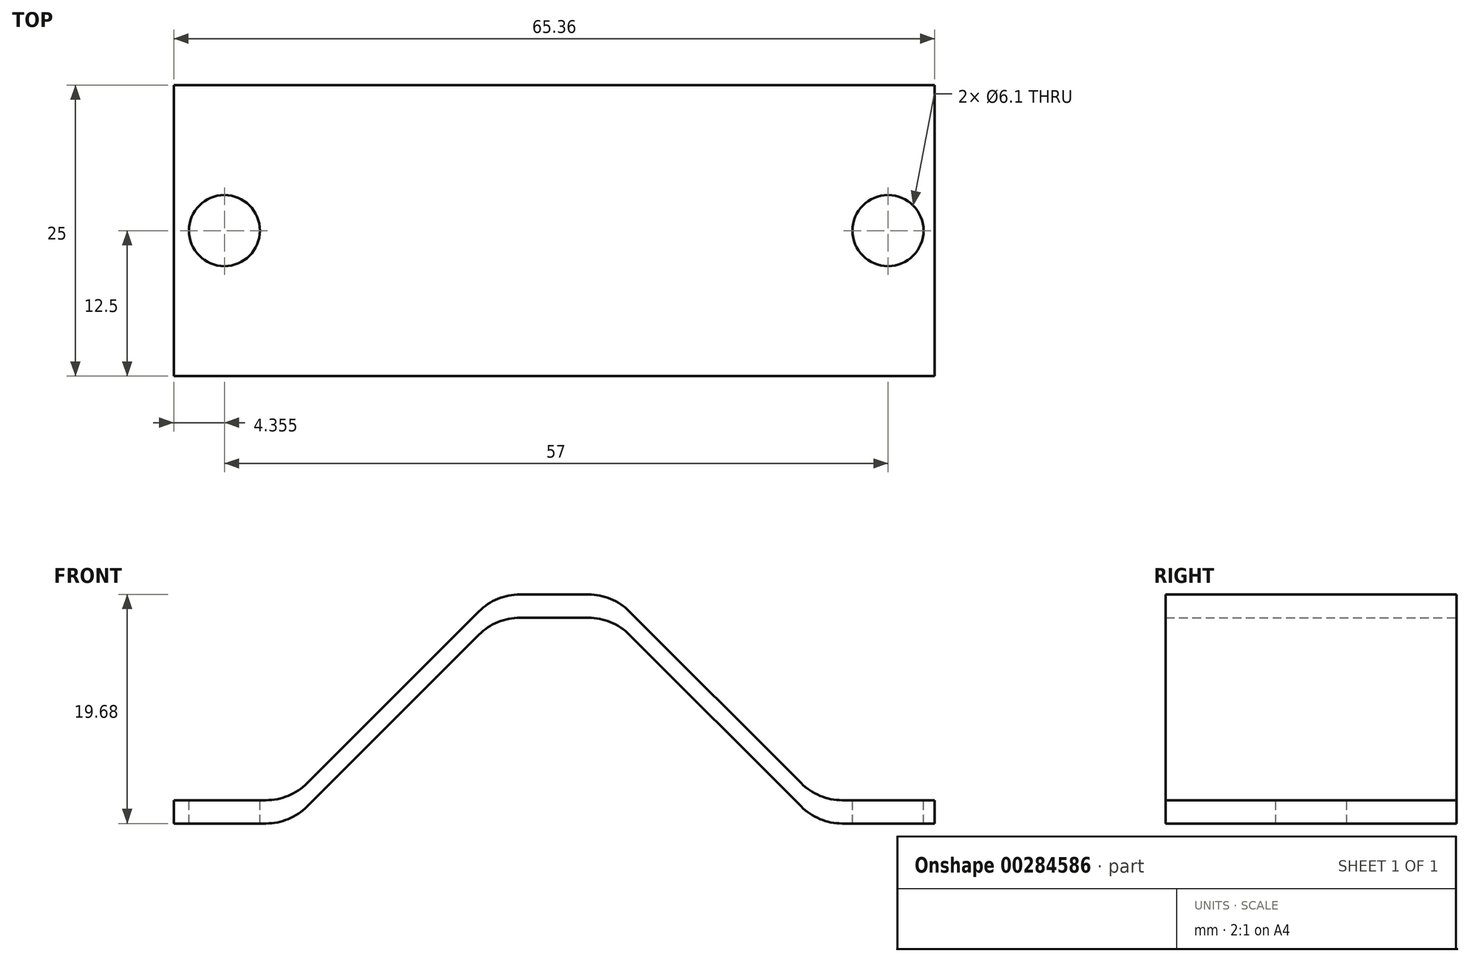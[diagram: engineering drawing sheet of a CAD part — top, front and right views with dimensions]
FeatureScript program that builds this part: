
annotation { "Feature Type Name" : "Feature", "Feature Type Description" : "" }
export const myFeature = defineFeature(function(context is Context, id is Id, definition is map)
    precondition{}
    {
        {
            var Q0;
            Q0=qCreatedBy(makeId("Front.planeOp"),FACE);
            var sketch = newSketch(context, id + "F0", { "sketchPlane" : qUnion([Q0])});
            skLineSegment(sketch, "E0", {"start": v(0, 0) * mm, "end": v(7.93, 0) * mm});
            skLineSegment(sketch, "E1", {"start": v(11.46, 1.46) * mm, "end": v(26.21, 16.21) * mm});
            skLineSegment(sketch, "E2", {"start": v(29.75, 17.68) * mm, "end": v(35.6, 17.68) * mm});
            skLineSegment(sketch, "E3", {"start": v(39.14, 16.21) * mm, "end": v(53.9, 1.46) * mm});
            skLineSegment(sketch, "E4", {"start": v(57.43, 0) * mm, "end": v(65.36, 0) * mm});
            skLineSegment(sketch, "E5", {"start": v(65.36, 0) * mm, "end": v(65.36, -2) * mm});
            skLineSegment(sketch, "E6", {"start": v(65.36, -2) * mm, "end": v(57.43, -2) * mm});
            skLineSegment(sketch, "E7", {"start": v(53.9, -0.54) * mm, "end": v(39.14, 14.21) * mm});
            skLineSegment(sketch, "E8", {"start": v(35.6, 15.68) * mm, "end": v(29.75, 15.68) * mm});
            skLineSegment(sketch, "E9", {"start": v(26.21, 14.21) * mm, "end": v(11.46, -0.54) * mm});
            skLineSegment(sketch, "E10", {"start": v(7.93, -2) * mm, "end": v(0, -2) * mm});
            skLineSegment(sketch, "E11", {"start": v(0, -2) * mm, "end": v(0, 0) * mm});
            skPoint(sketch, "E12.visualSharp", {"position": v(27.68, 15.68) * mm});
            skArc(sketch, "E12.filletArc", {"start": v(29.75, 15.68) * mm, "mid": v(27.84, 15.3) * mm, "end": v(26.21, 14.21) * mm});
            skPoint(sketch, "E13.visualSharp", {"position": v(27.68, 17.68) * mm});
            skArc(sketch, "E13.filletArc", {"start": v(29.75, 17.68) * mm, "mid": v(27.84, 17.3) * mm, "end": v(26.21, 16.21) * mm});
            skPoint(sketch, "E14.visualSharp", {"position": v(37.68, 15.68) * mm});
            skArc(sketch, "E14.filletArc", {"start": v(39.14, 14.21) * mm, "mid": v(37.52, 15.3) * mm, "end": v(35.6, 15.68) * mm});
            skPoint(sketch, "E15.visualSharp", {"position": v(37.68, 17.68) * mm});
            skArc(sketch, "E15.filletArc", {"start": v(39.14, 16.21) * mm, "mid": v(37.52, 17.3) * mm, "end": v(35.6, 17.68) * mm});
            skPoint(sketch, "E16.visualSharp", {"position": v(10, 0) * mm});
            skArc(sketch, "E16.filletArc", {"start": v(7.93, 0) * mm, "mid": v(9.84, 0.38) * mm, "end": v(11.46, 1.46) * mm});
            skPoint(sketch, "E17.visualSharp", {"position": v(10, -2) * mm});
            skArc(sketch, "E17.filletArc", {"start": v(7.93, -2) * mm, "mid": v(9.84, -1.62) * mm, "end": v(11.46, -0.54) * mm});
            skPoint(sketch, "E18.visualSharp", {"position": v(55.36, -2) * mm});
            skArc(sketch, "E18.filletArc", {"start": v(53.9, -0.54) * mm, "mid": v(55.51, -1.62) * mm, "end": v(57.43, -2) * mm});
            skPoint(sketch, "E19.visualSharp", {"position": v(55.36, 0) * mm});
            skArc(sketch, "E19.filletArc", {"start": v(53.9, 1.46) * mm, "mid": v(55.51, 0.38) * mm, "end": v(57.43, 0) * mm});
            skSolve(sketch);
        }
        {
            var Q0;
            Q0=makeQuery(id+"F0.imprint","IMPRINT",FACE,{"disambiguationData":[TD([[makeQuery(id+"F0.imprint","IMPRINT",EDGE,{"derivedFrom":sQuery(id+"F0.wireOp",EDGE,"E0")}),-1.0]])]});
            extrude(context, id + "F1", {"entities" : qUnion([Q0]), "depth" : 25 * mm});
        }
        {
            var Q0;
            Q0=makeQuery(id+"F1.opExtrude","SWEPT_FACE",FACE,{"disambiguationData":[OSD([sQuery(id+"F0.wireOp",EDGE,"E4")])]});
            var sketch = newSketch(context, id + "F2", { "sketchPlane" : qUnion([Q0])});
            skLineSegment(sketch, "E20", {"start": v(65.36, -12.5) * mm, "end": v(61.36, -12.5) * mm, "construction": true});
            skLineSegment(sketch, "E21", {"start": v(0, 0) * mm, "end": v(0, -12.5) * mm, "construction": true});
            skLineSegment(sketch, "E22", {"start": v(0, -12.5) * mm, "end": v(4.36, -12.5) * mm, "construction": true});
            skPoint(sketch, "E23", {"position": v(4.36, -12.5) * mm});
            skPoint(sketch, "E24", {"position": v(61.36, -12.5) * mm});
            skSolve(sketch);
        }
        {
            var Q0;
            Q0=sQuery(id+"F2.wireOp",VERTEX,"E23");
            var Q1;
            Q1=sQuery(id+"F2.wireOp",VERTEX,"E24");
            var Q2;
            Q2=makeQuery(id+"F1.opExtrude","SWEPT_BODY",BODY,{"disambiguationData":[OSD([sQuery(id+"F0.wireOp",EDGE,"E0"),sQuery(id+"F0.wireOp",EDGE,"E1"),sQuery(id+"F0.wireOp",EDGE,"E2"),sQuery(id+"F0.wireOp",EDGE,"E3"),sQuery(id+"F0.wireOp",EDGE,"E4"),sQuery(id+"F0.wireOp",EDGE,"E5"),sQuery(id+"F0.wireOp",EDGE,"E6"),sQuery(id+"F0.wireOp",EDGE,"E7"),sQuery(id+"F0.wireOp",EDGE,"E8"),sQuery(id+"F0.wireOp",EDGE,"E9"),sQuery(id+"F0.wireOp",EDGE,"E10"),sQuery(id+"F0.wireOp",EDGE,"E11"),sQuery(id+"F0.wireOp",EDGE,"E12.filletArc"),sQuery(id+"F0.wireOp",EDGE,"E13.filletArc"),sQuery(id+"F0.wireOp",EDGE,"E14.filletArc"),sQuery(id+"F0.wireOp",EDGE,"E15.filletArc"),sQuery(id+"F0.wireOp",EDGE,"E16.filletArc"),sQuery(id+"F0.wireOp",EDGE,"E17.filletArc"),sQuery(id+"F0.wireOp",EDGE,"E18.filletArc"),sQuery(id+"F0.wireOp",EDGE,"E19.filletArc")])]});
            hole(context, id + "F3", {"style" : HoleStyle.SIMPLE, "endStyle" : HoleEndStyle.THROUGH, "holeDiameter" : 6.1 * mm, "locations" : qUnion([Q0, Q1]), "scope" : qUnion([Q2]), "isTappedThrough" : true});
        }
    });
